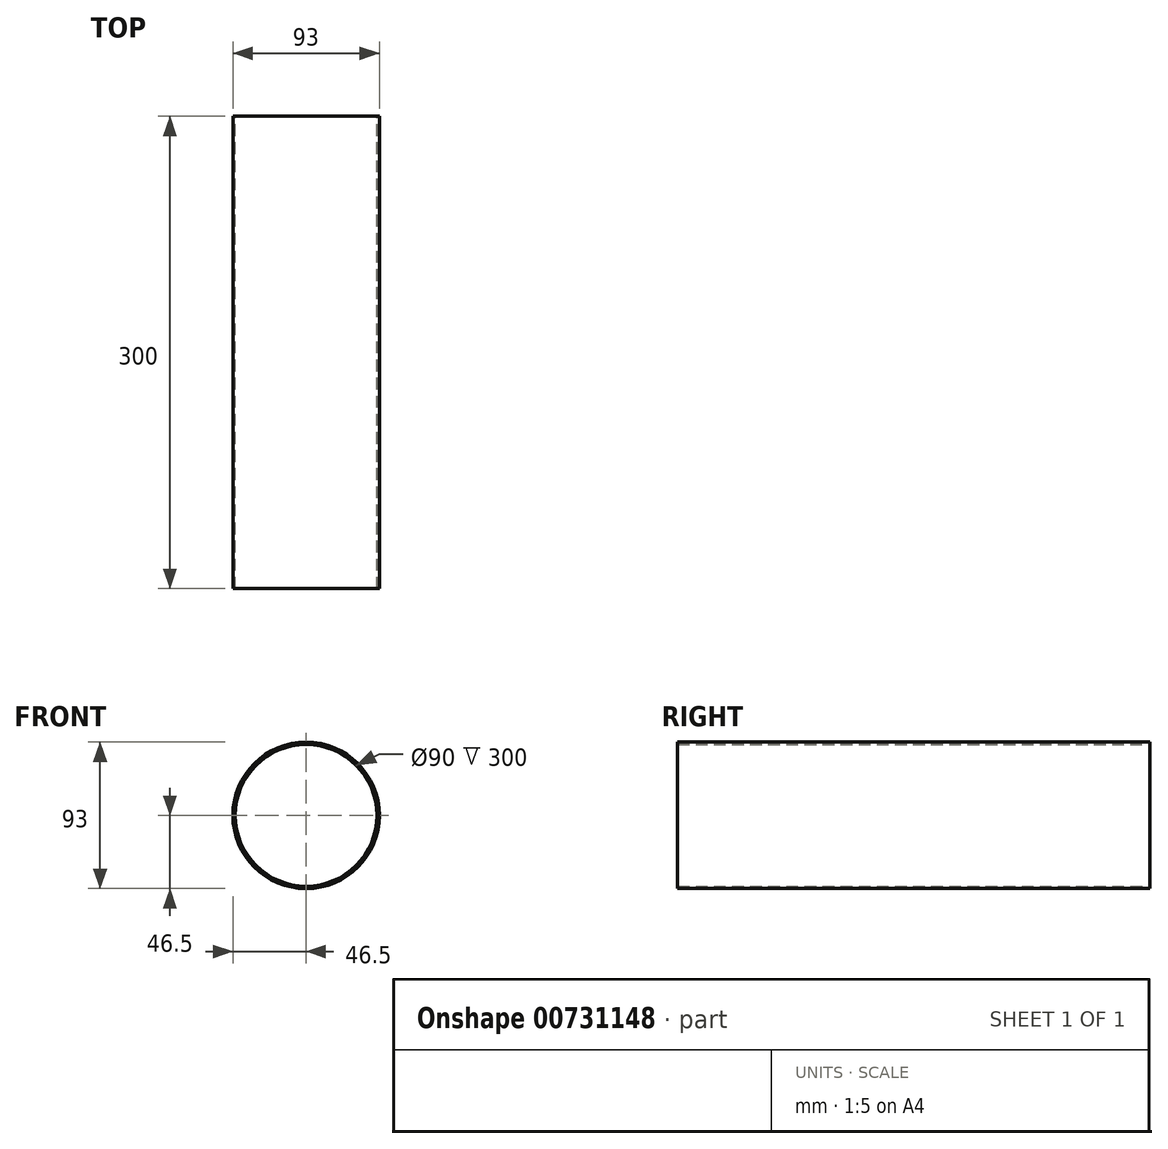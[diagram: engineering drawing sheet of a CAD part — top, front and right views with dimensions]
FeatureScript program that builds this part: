
annotation { "Feature Type Name" : "Feature", "Feature Type Description" : "" }
export const myFeature = defineFeature(function(context is Context, id is Id, definition is map)
    precondition{}
    {
        {
            var Q0;
            Q0=qCreatedBy(makeId("Front.planeOp"),FACE);
            var sketch = newSketch(context, id + "F0", { "sketchPlane" : qUnion([Q0])});
            skCircle(sketch, "E0", {"center": v(0, 0) * mm, "radius": 45 * mm});
            skCircle(sketch, "E1", {"center": v(0, 0) * mm, "radius": 46.5 * mm});
            skSolve(sketch);
        }
        {
            var Q0;
            Q0=qSketchRegion(id+"F0",true);
            extrude(context, id + "F1", {"entities" : qUnion([Q0]), "depth" : 300 * mm, "offsetDistance" : 25 * mm});
        }
    });
